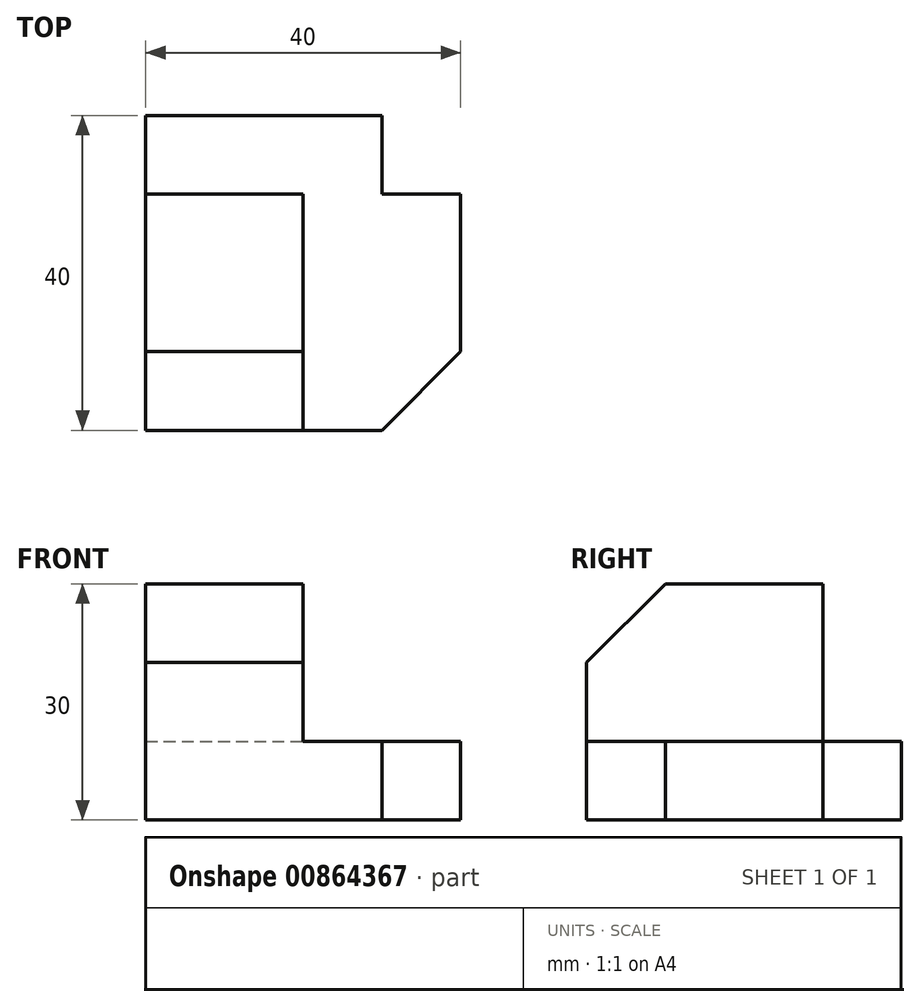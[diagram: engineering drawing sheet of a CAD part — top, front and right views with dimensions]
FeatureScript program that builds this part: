
annotation { "Feature Type Name" : "Feature", "Feature Type Description" : "" }
export const myFeature = defineFeature(function(context is Context, id is Id, definition is map)
    precondition{}
    {
        {
            var Q0;
            Q0=qCreatedBy(makeId("Top.planeOp"),FACE);
            var sketch = newSketch(context, id + "F0", { "sketchPlane" : qUnion([Q0])});
            skLineSegment(sketch, "E0.bottom", {"start": v(0, 0) * mm, "end": v(30, 0) * mm});
            skLineSegment(sketch, "E0.top", {"start": v(0, 40) * mm, "end": v(30, 40) * mm});
            skLineSegment(sketch, "E0.left", {"start": v(0, 0) * mm, "end": v(0, 40) * mm});
            skLineSegment(sketch, "E0.right", {"start": v(30, 0) * mm, "end": v(30, 40) * mm});
            skLineSegment(sketch, "E1.bottom", {"start": v(0, 0) * mm, "end": v(20, 0) * mm});
            skLineSegment(sketch, "E1.top", {"start": v(0, 30) * mm, "end": v(20, 30) * mm});
            skLineSegment(sketch, "E1.left", {"start": v(0, 0) * mm, "end": v(0, 30) * mm});
            skLineSegment(sketch, "E1.right", {"start": v(20, 0) * mm, "end": v(20, 30) * mm});
            skLineSegment(sketch, "E2.bottom", {"start": v(30, 0) * mm, "end": v(40, 0) * mm});
            skLineSegment(sketch, "E2.top", {"start": v(30, 30) * mm, "end": v(40, 30) * mm});
            skLineSegment(sketch, "E2.left", {"start": v(30, 0) * mm, "end": v(30, 30) * mm});
            skLineSegment(sketch, "E2.right", {"start": v(40, 0) * mm, "end": v(40, 30) * mm});
            skSolve(sketch);
        }
        {
            var Q0;
            {var subQ4=sQuery(id+"F0.wireOp",EDGE,"E1.top");Q0=makeQuery(id+"F0.imprint","IMPRINT",FACE,{"disambiguationData":[TD([[makeQuery(id+"F0.imprint","IMPRINT",EDGE,{"derivedFrom":subQ4}),-1.0]])]});}
            var Q1;
            {var subQ5=sQuery(id+"F0.wireOp",EDGE,"E0.top");Q1=makeQuery(id+"F0.imprint","IMPRINT",FACE,{"disambiguationData":[TD([[makeQuery(id+"F0.imprint","IMPRINT",EDGE,{"derivedFrom":subQ5}),-1.0]])]});}
            var Q2;
            {var subQ0=sQuery(id+"F0.wireOp",EDGE,"E2.bottom");Q2=makeQuery(id+"F0.imprint","IMPRINT",FACE,{"disambiguationData":[TD([[makeQuery(id+"F0.imprint","IMPRINT",EDGE,{"derivedFrom":subQ0}),1.0]])]});}
            extrude(context, id + "F1", {"entities" : qUnion([Q0, Q1, Q2]), "oppositeDirection" : true, "depth" : 10 * mm, "offsetDistance" : 25 * mm});
        }
        {
            var Q0;
            {var subQ4=sQuery(id+"F0.wireOp",EDGE,"E1.top");Q0=makeQuery(id+"F0.imprint","IMPRINT",FACE,{"disambiguationData":[TD([[makeQuery(id+"F0.imprint","IMPRINT",EDGE,{"derivedFrom":subQ4}),-1.0]])]});}
            extrude(context, id + "F2", {"entities" : qUnion([Q0]), "operationType" : NewBodyOperationType.ADD, "depth" : 20 * mm, "offsetDistance" : 25 * mm});
        }
        {
            var Q0;
            Q0=makeQuery(id+"F2.opExtrude","CAP_EDGE",EDGE,{"disambiguationData":[OSD([sQuery(id+"F0.wireOp",EDGE,"E0.bottom")])],"isStart":false});
            chamfer(context, id + "F3", {"entities" : qUnion([Q0]), "chamferType" : ChamferType.OFFSET_ANGLE, "width" : 10 * mm, "oppositeDirection" : false, "angle" : 45 * degree, "tangentPropagation" : true});
        }
        {
            var Q0;
            Q0=makeQuery(id+"F1.opExtrude","SWEPT_EDGE",EDGE,{"disambiguationData":[OSD([sQuery(id+"F0.wireOp",EDGE,"E2.bottom"),sQuery(id+"F0.wireOp",EDGE,"E2.right")])]});
            chamfer(context, id + "F4", {"entities" : qUnion([Q0]), "chamferType" : ChamferType.OFFSET_ANGLE, "width" : 10 * mm, "oppositeDirection" : false, "angle" : 45 * degree, "tangentPropagation" : true});
        }
    });
